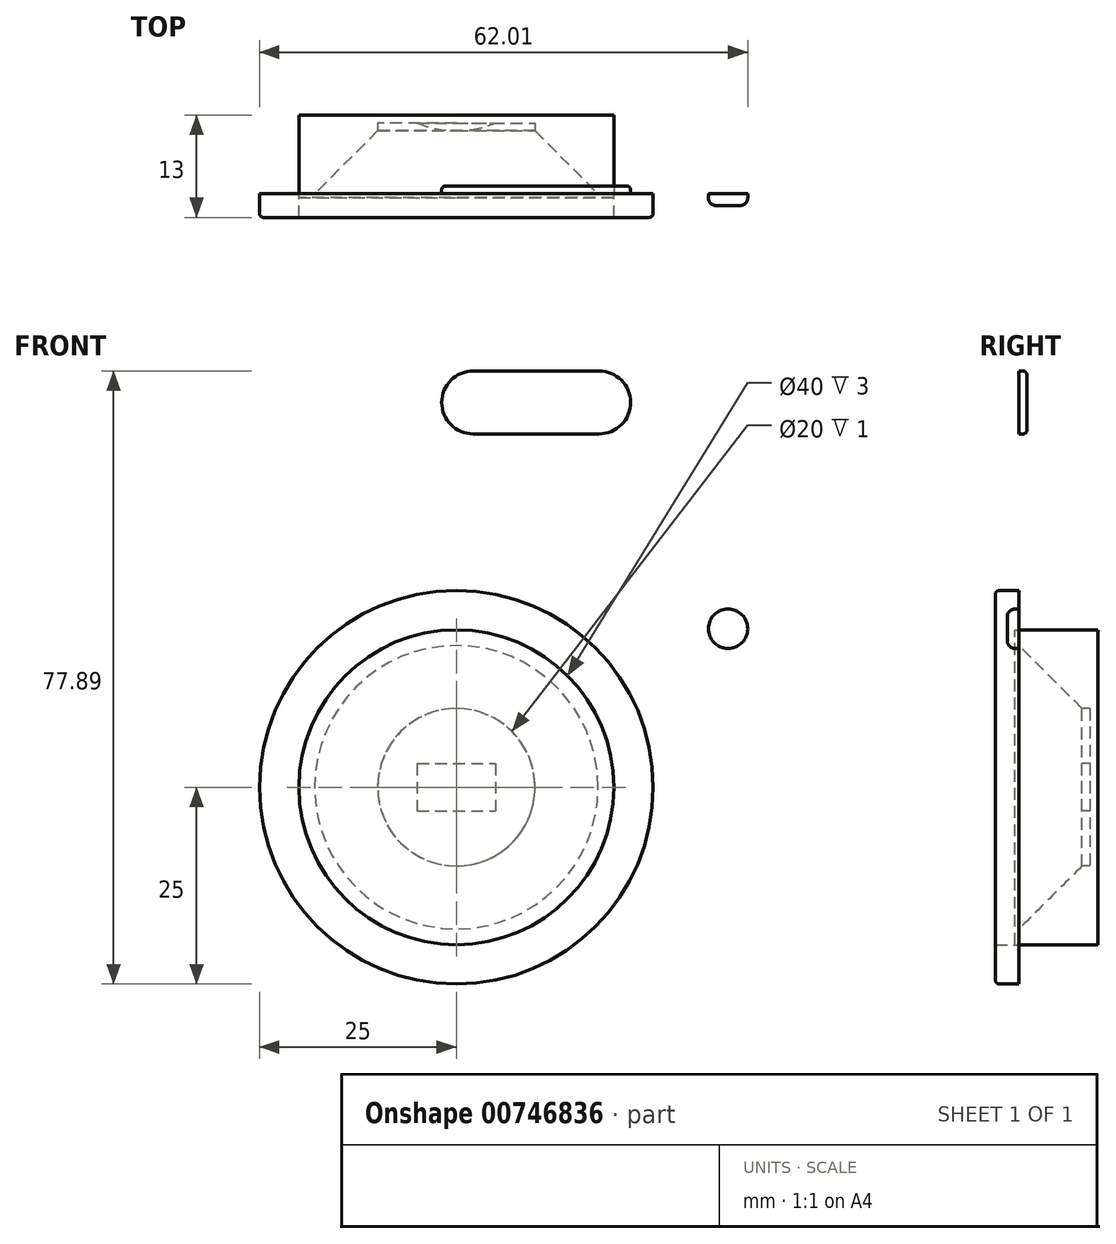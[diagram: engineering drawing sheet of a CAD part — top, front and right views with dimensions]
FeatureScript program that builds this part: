
annotation { "Feature Type Name" : "Feature", "Feature Type Description" : "" }
export const myFeature = defineFeature(function(context is Context, id is Id, definition is map)
    precondition{}
    {
        {
            var Q0;
            Q0=qCreatedBy(makeId("Front.planeOp"),FACE);
            var sketch = newSketch(context, id + "F0", { "sketchPlane" : qUnion([Q0])});
            skCircle(sketch, "E0", {"center": v(0, 0) * mm, "radius": 25 * mm});
            skCircle(sketch, "E1", {"center": v(0, 0) * mm, "radius": 20 * mm});
            skCircle(sketch, "E2", {"center": v(0, 0) * mm, "radius": 10 * mm});
            skCircle(sketch, "E3", {"center": v(34.5, 20.14) * mm, "radius": 2.5 * mm});
            skSolve(sketch);
        }
        {
            var Q0;
            Q0=makeQuery(id+"F0.imprint","IMPRINT",FACE,{"disambiguationData":[TD([[makeQuery(id+"F0.imprint","IMPRINT",EDGE,{"derivedFrom":sQuery(id+"F0.wireOp",EDGE,"E1")}),1.0]])]});
            extrude(context, id + "F1", {"entities" : qUnion([Q0]), "depth" : -10 * mm, "offsetDistance" : 25 * mm});
        }
        {
            var Q0;
            Q0=makeQuery(id+"F1.opExtrude","CAP_EDGE",EDGE,{"disambiguationData":[OSD([sQuery(id+"F0.wireOp",EDGE,"E2")])],"isStart":true});
            chamfer(context, id + "F2", {"entities" : qUnion([Q0]), "width" : 8 * mm, "tangentPropagation" : true});
        }
        {
            var Q0;
            Q0=makeQuery(id+"F0.imprint","IMPRINT",FACE,{"disambiguationData":[TD([[makeQuery(id+"F0.imprint","IMPRINT",EDGE,{"derivedFrom":sQuery(id+"F0.wireOp",EDGE,"E0")}),1.0]])]});
            extrude(context, id + "F3", {"entities" : qUnion([Q0]), "depth" : 3 * mm, "offsetDistance" : 25 * mm});
        }
        {
            var Q0;
            Q0=makeQuery(id+"F0.imprint","IMPRINT",FACE,{"disambiguationData":[TD([[makeQuery(id+"F0.imprint","IMPRINT",EDGE,{"derivedFrom":sQuery(id+"F0.wireOp",EDGE,"E1")}),1.0]])]});
            var Q1;
            Q1=makeQuery(id+"F0.imprint","IMPRINT",FACE,{"disambiguationData":[TD([[makeQuery(id+"F0.imprint","IMPRINT",EDGE,{"derivedFrom":sQuery(id+"F0.wireOp",EDGE,"E2")}),1.0]])]});
            var Q2;
            Q2=makeQuery(id+"F0.imprint","IMPRINT",FACE,{"disambiguationData":[TD([[makeQuery(id+"F0.imprint","IMPRINT",EDGE,{"derivedFrom":sQuery(id+"F0.wireOp",EDGE,"6b22d815-0cee-402b-a612-9939516ca7fd.bottom")}),1.0]])]});
            var Q3;
            Q3=sQuery(id+"F0.wireOp",EDGE,"E1");
            extrude(context, id + "F4", {"entities" : qUnion([Q0, Q1, Q2]), "surfaceEntities" : qUnion([Q3]), "depth" : 0.5 * mm, "offsetDistance" : 25 * mm});
        }
        {
            var Q0;
            Q0=makeQuery(id+"F1.opExtrude","CAP_FACE",FACE,{"disambiguationData":[OSD([sQuery(id+"F0.wireOp",EDGE,"E1"),sQuery(id+"F0.wireOp",EDGE,"E2")])],"isStart":false});
            var sketch = newSketch(context, id + "F5", { "sketchPlane" : qUnion([Q0])});
            skLineSegment(sketch, "E4.bottom", {"start": v(5, 3) * mm, "end": v(-5, 3) * mm});
            skLineSegment(sketch, "E4.top", {"start": v(5, -3) * mm, "end": v(-5, -3) * mm});
            skLineSegment(sketch, "E4.left", {"start": v(5, 3) * mm, "end": v(5, -3) * mm});
            skLineSegment(sketch, "E4.right", {"start": v(-5, 3) * mm, "end": v(-5, -3) * mm});
            skPoint(sketch, "E4.middle", {"position": v(0, 0) * mm});
            skCircle(sketch, "E5", {"center": v(0, 0) * mm, "radius": 10 * mm});
            skSolve(sketch);
        }
        {
            var Q0;
            Q0=makeQuery(id+"F5.imprint","IMPRINT",FACE,{"disambiguationData":[TD([[makeQuery(id+"F5.imprint","IMPRINT",EDGE,{"derivedFrom":sQuery(id+"F5.wireOp",EDGE,"E4.bottom")}),-1.0]])]});
            extrude(context, id + "F6", {"entities" : qUnion([Q0]), "operationType" : NewBodyOperationType.ADD, "depth" : -1 * mm, "offsetDistance" : 25 * mm});
        }
        {
            var Q0;
            Q0=makeQuery(id+"F5.imprint","IMPRINT",FACE,{"disambiguationData":[TD([[makeQuery(id+"F5.imprint","IMPRINT",EDGE,{"derivedFrom":sQuery(id+"F5.wireOp",EDGE,"E4.bottom")}),1.0]])]});
            extrude(context, id + "F7", {"entities" : qUnion([Q0]), "operationType" : NewBodyOperationType.ADD, "depth" : -2 * mm, "offsetDistance" : 25 * mm});
        }
        {
            var Q0;
            Q0=makeQuery(id+"F7.opExtrude","CAP_EDGE",EDGE,{"disambiguationData":[OSD([sQuery(id+"F5.wireOp",EDGE,"E4.left")])],"isStart":false});
            var Q1;
            Q1=makeQuery(id+"F7.opExtrude","CAP_EDGE",EDGE,{"disambiguationData":[OSD([sQuery(id+"F5.wireOp",EDGE,"E4.right")])],"isStart":false});
            fillet(context, id + "F8", {"entities" : qUnion([Q0, Q1]), "radius" : 13 * mm, "tangentPropagation" : true, "allowEdgeOverflow" : false});
        }
        {
            var Q0;
            Q0=makeQuery(id+"F3.opExtrude","CAP_EDGE",EDGE,{"disambiguationData":[OSD([sQuery(id+"F0.wireOp",EDGE,"E0")])],"isStart":false});
            fillet(context, id + "F9", {"entities" : qUnion([Q0]), "radius" : 0.5 * mm, "tangentPropagation" : true, "allowEdgeOverflow" : false});
        }
        {
            var Q0;
            Q0=makeQuery(id+"F0.imprint","IMPRINT",FACE,{"disambiguationData":[TD([[makeQuery(id+"F0.imprint","IMPRINT",EDGE,{"derivedFrom":sQuery(id+"F0.wireOp",EDGE,"E3")}),1.0]])]});
            extrude(context, id + "F10", {"entities" : qUnion([Q0]), "depth" : 1.5 * mm, "offsetDistance" : 25 * mm});
        }
        {
            var Q0;
            Q0=makeQuery(id+"F10.opExtrude","CAP_EDGE",EDGE,{"disambiguationData":[OSD([sQuery(id+"F0.wireOp",EDGE,"E3")])],"isStart":false});
            fillet(context, id + "F11", {"entities" : qUnion([Q0]), "radius" : 1 * mm, "tangentPropagation" : true, "allowEdgeOverflow" : false});
        }
        {
            var Q0;
            Q0=qCreatedBy(makeId("Front.planeOp"),FACE);
            var sketch = newSketch(context, id + "F12", { "sketchPlane" : qUnion([Q0])});
            skPoint(sketch, "E6.middle", {"position": v(10.13, 17.96) * mm});
            skPoint(sketch, "E7.middle", {"position": v(10.13, 48.89) * mm});
            skLineSegment(sketch, "E8.bottom", {"start": v(18.13, 52.89) * mm, "end": v(2.13, 52.89) * mm});
            skLineSegment(sketch, "E8.top", {"start": v(18.13, 44.89) * mm, "end": v(2.13, 44.89) * mm});
            skLineSegment(sketch, "E8.left", {"start": v(18.13, 52.89) * mm, "end": v(18.13, 44.89) * mm});
            skLineSegment(sketch, "E8.right", {"start": v(2.13, 52.89) * mm, "end": v(2.13, 44.89) * mm});
            skCircle(sketch, "E9", {"center": v(18.13, 48.89) * mm, "radius": 4 * mm});
            skCircle(sketch, "E10", {"center": v(2.13, 48.89) * mm, "radius": 4 * mm});
            skSolve(sketch);
        }
        {
            var Q0;
            {var subQ0=sQuery(id+"F12.wireOp",EDGE,"E8.left");Q0=makeQuery(id+"F12.imprint","IMPRINT",FACE,{"disambiguationData":[TD([[makeQuery(id+"F12.imprint","IMPRINT",EDGE,{"derivedFrom":subQ0}),1.0]])]});}
            var Q1;
            {var subQ0=sQuery(id+"F12.wireOp",EDGE,"E8.left");Q1=makeQuery(id+"F12.imprint","IMPRINT",FACE,{"disambiguationData":[TD([[makeQuery(id+"F12.imprint","IMPRINT",EDGE,{"derivedFrom":subQ0}),-1.0]])]});}
            var Q2;
            {var subQ0=sQuery(id+"F12.wireOp",EDGE,"E8.bottom");Q2=makeQuery(id+"F12.imprint","IMPRINT",FACE,{"disambiguationData":[TD([[makeQuery(id+"F12.imprint","IMPRINT",EDGE,{"derivedFrom":subQ0}),1.0]])]});}
            var Q3;
            {var subQ0=sQuery(id+"F12.wireOp",EDGE,"E8.right");Q3=makeQuery(id+"F12.imprint","IMPRINT",FACE,{"disambiguationData":[TD([[makeQuery(id+"F12.imprint","IMPRINT",EDGE,{"derivedFrom":subQ0}),1.0]])]});}
            var Q4;
            {var subQ0=sQuery(id+"F12.wireOp",EDGE,"E8.right");Q4=makeQuery(id+"F12.imprint","IMPRINT",FACE,{"disambiguationData":[TD([[makeQuery(id+"F12.imprint","IMPRINT",EDGE,{"derivedFrom":subQ0}),-1.0]])]});}
            extrude(context, id + "F13", {"entities" : qUnion([Q0, Q1, Q2, Q3, Q4]), "depth" : -1 * mm, "offsetDistance" : 25 * mm});
        }
        {
            var Q0;
            Q0=makeQuery(id+"F13.opExtrude","CAP_FACE",FACE,{"disambiguationData":[OSD([sQuery(id+"F12.wireOp",EDGE,"E8.bottom"),sQuery(id+"F12.wireOp",EDGE,"E8.top"),sQuery(id+"F12.wireOp",EDGE,"E9"),sQuery(id+"F12.wireOp",EDGE,"E10")])],"isStart":false});
            fillet(context, id + "F14", {"entities" : qUnion([Q0]), "radius" : 0.5 * mm, "tangentPropagation" : true, "allowEdgeOverflow" : false});
        }
    });
